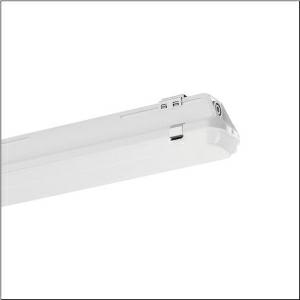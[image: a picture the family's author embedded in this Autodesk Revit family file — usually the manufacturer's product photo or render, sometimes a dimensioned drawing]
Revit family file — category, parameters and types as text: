
# Revit family: monsun_11_51fp10ep430l007
name_source: partatom
category: Lighting Fixtures
units: mm (PartAtom-declared; Revit-internal decimal feet)

## family parameters
Cut with Voids When Loaded = No
Host = Face
Light Source = No
Part Type = Normal
Room Calculation Point = No
Round Connector Dimension = Use Diameter
Shared = No

## types (1)
- --- (1 x LED, 3840 lm, 20.5 W, 4000K)
    Apparent Load = 21 VA
    CIE Flux Codes = 47 77 93 94 100
    Color Rendering = 80
    Color Temperature = 4000K
    Default Elevation = 1800 mm
    Description = Monsun 11, damp-proof luminaire, chain hanger, primary optical cover: enclosure, of PMMA, light emission: direct distribution, primary light characteristic: symmetric, installation type: suspended mounting, surface-mounted, horizontal mounting, vertical mounting, LED, rated luminous flux: 3.840lm, luminous efficacy: 187lm/W, light colour: 840, colour temperature: 4000K, control gear: DALI 2, with terminal, 5-pole, max. 2.5mm², through-wiring: 7x 2.5mm², mains connection: 220..240V, AC, 50/60Hz, rated input power: 21W, housing, of glass-fibre reinforced polyester, uncoated, bright grey, incl. chain hanger, length: 1.590mm, width: 90mm, height: 88mm, clip for enclosure, of stainless steel (V2A), ceiling mounting element, of stainless steel (V2A), chain hanger, of stainless steel (V2A), protection rating (complete): IP66, insulation class (complete): insulation class I (protective earthing), certification: CE, ENEC, VDE, UKCA, protection symbol: D, impact resistance: IK04, permissible operating ambient temperature: -25..+35°C, standard: EN 50419, EN 60598-2-1, corresponds to IFS (International Featured Standards) requirements for safety and quality in the food industry, for indoor or canopied outdoor use, no direct snow, no direct sun, no direct rain, LABS conformity tested according to VDMA 24364:2018-05, contact your sales advisor before using the luminaires in applications with unclear chemical exposure, large temperature fluctuations or condensation-forming humidity, packaging unit: 1 piece
    Height = 89 mm
    Lamp = 1 x LED
    Lamp Light Flux = 3840 lm
    Lamp Power = 20.5 W
    Lamp count = 1
    Length = 1590 mm
    Luminous efficacy = 187 lm/W
    Manufacturer = Siteco
    ModVariant = No
    Model = 51FP10EP430L007
    Mounting Place = Ceiling
    Mounting Type = Surface mounted
    Number of Poles = 1
    OnlyDefault = Yes
    Power Factor = 1
    Product Name = Monsun 11
    Product group = damp-proof luminaire
    ProductGroupID = 300
    Protection Class = Protection class I
    Protection Degree = IP 66
    RLX_Detail_Level = 1
    RLX_Emergency_Light_Flux = 0 lm
    RLX_Emergency_Type = 0
    RLX_Emergency_Type_DB = No
    RlxData = <blob elided: 91765 chars, md5=921319c3>
    Socket = socket
    Standby Power = 0 W
    System Light Flux = 3840 lm
    System Power = 21 W
    Type Comments = factory setting: luminous flux: 100 % | dim-lin: 254 | 136 mA
    Type Image = l_1349237.jpg
    URL = http://relux.com
    VarID = @adj_033769
    Voltage = 0 V
    Weight = 0.00 kg
    Width = 90 mm

## geometry (parser evidence)
native form markers: Blend x4, Sweep x12
no freeform markers — native parametric forms only
